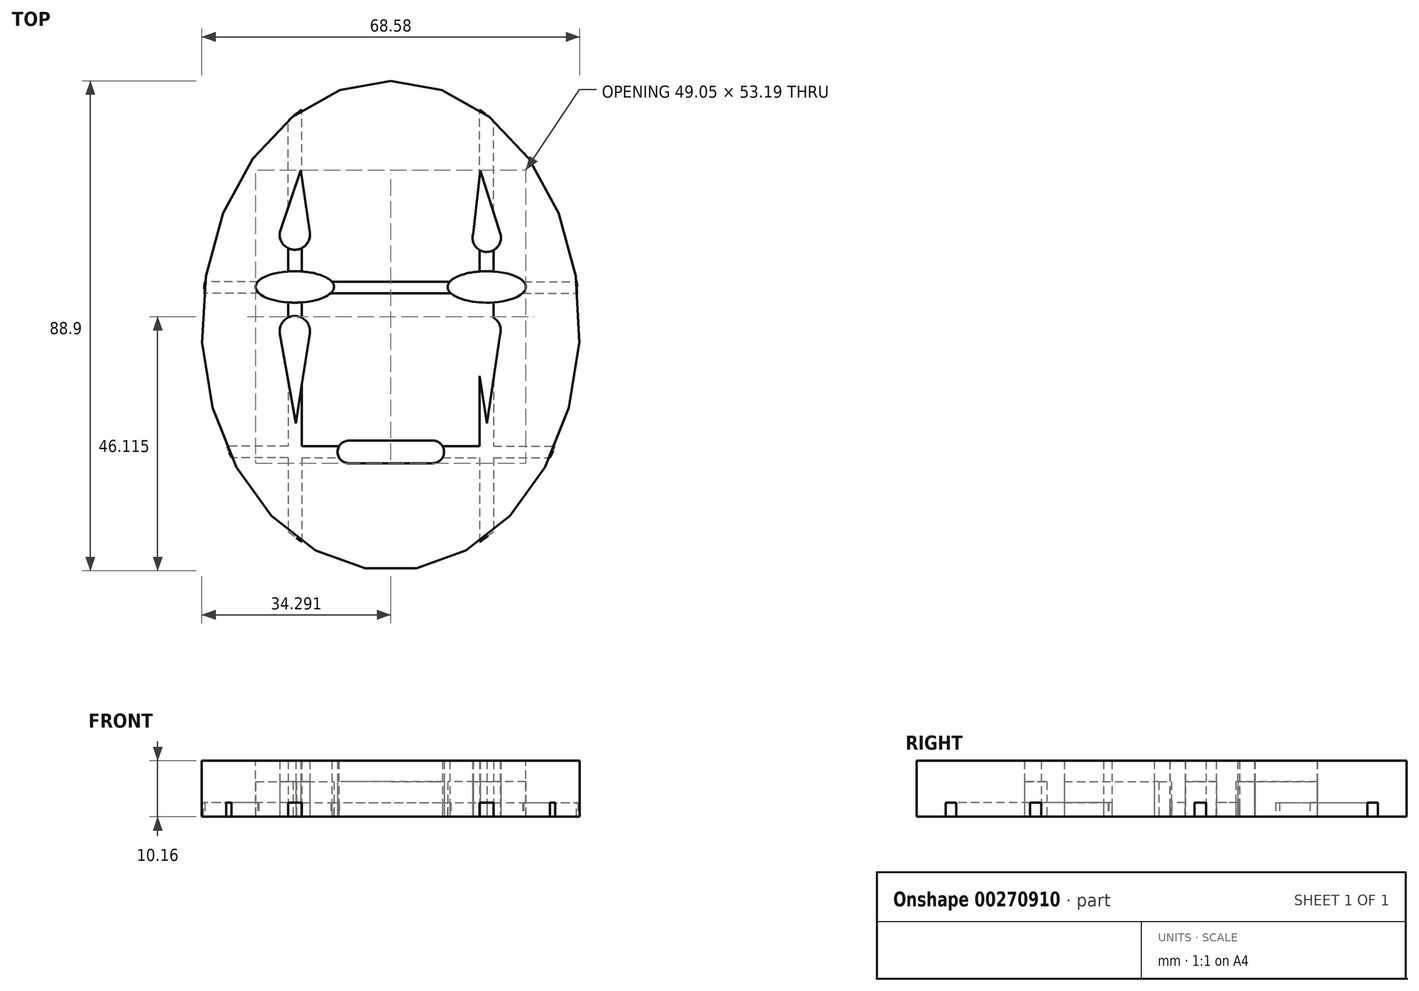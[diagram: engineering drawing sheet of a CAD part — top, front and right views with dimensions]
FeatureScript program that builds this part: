
annotation { "Feature Type Name" : "Feature", "Feature Type Description" : "" }
export const myFeature = defineFeature(function(context is Context, id is Id, definition is map)
    precondition{}
    {
        {
            var Q0;
            Q0=qCreatedBy(makeId("Top.planeOp"),FACE);
            var sketch = newSketch(context, id + "F0", { "sketchPlane" : qUnion([Q0])});
            skEllipse(sketch, "E0", {"center": v(0.89, 1.57) * mm, "majorRadius": 44.45 * mm, "minorRadius": 34.3 * mm, "majorAxis": v(0, 1)});
            skEllipse(sketch, "E1", {"center": v(-16.53, 8.64) * mm, "majorRadius": 7.1 * mm, "minorRadius": 2.85 * mm, "majorAxis": v(-1, 0)});
            skEllipse(sketch, "E2.MirrorC", {"center": v(18.3, 8.64) * mm, "majorRadius": 7.1 * mm, "minorRadius": 2.85 * mm, "majorAxis": v(1, 0)});
            skLineSegment(sketch, "E3.MirrorCS", {"start": v(-15.43, 29.83) * mm, "end": v(-13.8, 18.52) * mm});
            skArc(sketch, "E4", {"start": v(-19.24, 18.52) * mm, "mid": v(-16.52, 15.38) * mm, "end": v(-13.8, 18.52) * mm});
            skLineSegment(sketch, "E5", {"start": v(15.84, 18.38) * mm, "end": v(17.15, 29.74) * mm});
            skLineSegment(sketch, "E6", {"start": v(20.76, 18.36) * mm, "end": v(17.15, 29.74) * mm});
            skArc(sketch, "E7", {"start": v(15.84, 18.38) * mm, "mid": v(18.29, 15) * mm, "end": v(20.76, 18.36) * mm});
            skLineSegment(sketch, "E8", {"start": v(-19.24, 18.52) * mm, "end": v(-15.43, 29.83) * mm});
            skPoint(sketch, "E9.trimOffspring.end.orphan", {"position": v(-33.4, 1.57) * mm});
            skPoint(sketch, "E10.start.orphan", {"position": v(35.18, 1.57) * mm});
            skLineSegment(sketch, "E11", {"start": v(-16.53, 3.36) * mm, "end": v(-16.53, 3.34) * mm});
            skLineSegment(sketch, "E12", {"start": v(-16.33, -16.13) * mm, "end": v(-19.24, 0.19) * mm});
            skLineSegment(sketch, "E13", {"start": v(-16.33, -16.13) * mm, "end": v(-13.8, 0.19) * mm});
            skLineSegment(sketch, "E14", {"start": v(18.3, -16.13) * mm, "end": v(15.84, 0.2) * mm});
            skLineSegment(sketch, "E15", {"start": v(18.3, -16.13) * mm, "end": v(20.76, 0.19) * mm});
            skArc(sketch, "E16", {"start": v(-13.8, 0.19) * mm, "mid": v(-16.53, 3.36) * mm, "end": v(-19.24, 0.19) * mm});
            skArc(sketch, "E17", {"start": v(20.76, 0.19) * mm, "mid": v(18.31, 3.34) * mm, "end": v(15.84, 0.2) * mm});
            skLineSegment(sketch, "E18.trimOffspring", {"start": v(18.3, 3.34) * mm, "end": v(18.3, 3.34) * mm});
            skLineSegment(sketch, "E19.trimOffspring", {"start": v(-13.8, 1.03) * mm, "end": v(-13.8, 0.19) * mm});
            skLineSegment(sketch, "E20.trimOffspring", {"start": v(-16.84, 3.34) * mm, "end": v(-16.22, 3.34) * mm});
            skLineSegment(sketch, "E21.trimOffspring", {"start": v(-19.24, 1.03) * mm, "end": v(-19.24, 0.19) * mm});
            skLineSegment(sketch, "E22.trimOffspring", {"start": v(15.84, 1.41) * mm, "end": v(15.84, 0.2) * mm});
            skLineSegment(sketch, "E23.trimOffspring", {"start": v(20.76, 1.42) * mm, "end": v(20.76, 0.19) * mm});
            skPoint(sketch, "E24", {"position": v(0.9, -19.26) * mm});
            skPoint(sketch, "E25", {"position": v(0.9, -23.36) * mm});
            skLineSegment(sketch, "E26", {"start": v(0.9, -19.26) * mm, "end": v(-6.73, -19.26) * mm});
            skLineSegment(sketch, "E27", {"start": v(0.9, -19.26) * mm, "end": v(8.51, -19.26) * mm});
            skLineSegment(sketch, "E28", {"start": v(0.9, -23.36) * mm, "end": v(-6.73, -23.36) * mm});
            skLineSegment(sketch, "E29", {"start": v(0.9, -23.36) * mm, "end": v(8.51, -23.36) * mm});
            skArc(sketch, "E30", {"start": v(-6.73, -19.26) * mm, "mid": v(-8.78, -21.31) * mm, "end": v(-6.73, -23.36) * mm});
            skArc(sketch, "E31", {"start": v(8.51, -23.36) * mm, "mid": v(10.56, -21.3) * mm, "end": v(8.51, -19.26) * mm});
            skPoint(sketch, "E32.orphan", {"position": v(0.89, 46.02) * mm});
            skPoint(sketch, "E33.orphan", {"position": v(0.89, -42.88) * mm});
            skFitSpline(sketch, "E34.0", {"points": [v(2.64, 46.75) * mm, v(0.89, 46.8) * mm, v(-0.86, 46.75) * mm, v(-3.18, 46.52) * mm, v(-6.04, 45.97) * mm, v(-9.38, 44.88) * mm, v(-12.62, 43.38) * mm, v(-15.72, 41.48) * mm, v(-18.66, 39.2) * mm, v(-20.97, 36.98) * mm, v(-22.72, 35.03) * mm, v(-23.97, 33.48) * mm, v(-25.17, 31.85) * mm, v(-26.67, 29.6) * mm, v(-28.37, 26.62) * mm, v(-30.12, 22.83) * mm, v(-31.57, 18.84) * mm, v(-32.71, 14.7) * mm, v(-33.54, 10.42) * mm, v(-33.97, 6.77) * mm, v(-34.14, 3.81) * mm, v(-34.18, 1.57) * mm, v(-34.14, -0.66) * mm, v(-33.97, -3.62) * mm, v(-33.54, -7.27) * mm, v(-32.71, -11.55) * mm, v(-31.57, -15.7) * mm, v(-30.12, -19.68) * mm, v(-28.37, -23.47) * mm, v(-26.67, -26.45) * mm, v(-25.17, -28.7) * mm, v(-23.97, -30.34) * mm, v(-22.72, -31.89) * mm, v(-20.97, -33.83) * mm, v(-18.66, -36.05) * mm, v(-15.72, -38.33) * mm, v(-12.62, -40.23) * mm, v(-9.38, -41.73) * mm, v(-6.04, -42.82) * mm, v(-3.18, -43.38) * mm, v(-0.86, -43.6) * mm, v(0.89, -43.66) * mm, v(2.64, -43.6) * mm, v(4.96, -43.38) * mm, v(7.81, -42.82) * mm, v(11.16, -41.73) * mm, v(14.4, -40.23) * mm, v(17.5, -38.33) * mm, v(20.44, -36.05) * mm, v(22.75, -33.83) * mm, v(24.5, -31.89) * mm, v(25.75, -30.34) * mm, v(26.94, -28.7) * mm, v(28.44, -26.45) * mm, v(30.14, -23.47) * mm, v(31.9, -19.68) * mm, v(33.34, -15.7) * mm, v(34.49, -11.55) * mm, v(35.32, -7.27) * mm, v(35.74, -3.62) * mm, v(35.91, -0.66) * mm, v(35.95, 1.57) * mm, v(35.91, 3.81) * mm, v(35.74, 6.77) * mm, v(35.32, 10.42) * mm, v(34.49, 14.7) * mm, v(33.34, 18.84) * mm, v(31.9, 22.83) * mm, v(30.14, 26.62) * mm, v(28.44, 29.6) * mm, v(26.94, 31.85) * mm, v(25.75, 33.48) * mm, v(24.5, 35.03) * mm, v(22.75, 36.98) * mm, v(20.44, 39.2) * mm, v(17.5, 41.48) * mm, v(14.4, 43.38) * mm, v(11.16, 44.88) * mm, v(7.81, 45.97) * mm, v(4.96, 46.52) * mm, v(2.64, 46.75) * mm, v(0.89, 46.8) * mm, v(-0.86, 46.75) * mm, v(2.64, 46.75) * mm]});
            skLineSegment(sketch, "E35", {"start": v(-23.23, 9.58) * mm, "end": v(-32.84, 9.58) * mm});
            skLineSegment(sketch, "E36", {"start": v(-23.05, 7.5) * mm, "end": v(-33.1, 7.5) * mm});
            skLineSegment(sketch, "E37", {"start": v(-15.23, 15.7) * mm, "end": v(-15.23, 11.44) * mm});
            skLineSegment(sketch, "E38", {"start": v(-17.75, 15.67) * mm, "end": v(-17.75, 11.45) * mm});
            skLineSegment(sketch, "E39", {"start": v(-15.23, 28.45) * mm, "end": v(-15.23, 40.8) * mm});
            skLineSegment(sketch, "E40", {"start": v(-17.75, 22.94) * mm, "end": v(-17.75, 38.89) * mm});
            skLineSegment(sketch, "E41.MirrorCS", {"start": v(17, 28.5) * mm, "end": v(17, 40.8) * mm});
            skLineSegment(sketch, "E42.MirrorCS", {"start": v(19.52, 22.26) * mm, "end": v(19.52, 38.89) * mm});
            skLineSegment(sketch, "E43.MirrorCS", {"start": v(17, 15.34) * mm, "end": v(17, 11.44) * mm});
            skLineSegment(sketch, "E44.MirrorCS", {"start": v(19.52, 15.3) * mm, "end": v(19.52, 11.45) * mm});
            skLineSegment(sketch, "E45", {"start": v(10.3, -20.3) * mm, "end": v(17, -20.3) * mm});
            skLineSegment(sketch, "E46", {"start": v(10.27, -22.35) * mm, "end": v(17, -22.35) * mm});
            skLineSegment(sketch, "E47.MirrorCS", {"start": v(-17.75, -20.3) * mm, "end": v(-28.96, -20.3) * mm});
            skLineSegment(sketch, "E48.trimOffspring", {"start": v(-17.75, -8.18) * mm, "end": v(-17.75, -20.3) * mm});
            skLineSegment(sketch, "E49.trimOffspring", {"start": v(-15.23, -9.02) * mm, "end": v(-15.23, -20.3) * mm});
            skLineSegment(sketch, "E50.trimOffspring", {"start": v(-15.23, 5.83) * mm, "end": v(-15.23, 3.03) * mm});
            skLineSegment(sketch, "E51.trimOffspring", {"start": v(-9.82, 9.58) * mm, "end": v(11.6, 9.58) * mm});
            skLineSegment(sketch, "E52.trimOffspring", {"start": v(-10, 7.5) * mm, "end": v(11.79, 7.5) * mm});
            skLineSegment(sketch, "E53.trimOffspring", {"start": v(-17.75, 5.83) * mm, "end": v(-17.75, 3.07) * mm});
            skLineSegment(sketch, "E54.trimOffspring", {"start": v(17, -7.48) * mm, "end": v(17, -20.3) * mm});
            skLineSegment(sketch, "E55.trimOffspring", {"start": v(19.52, -8.06) * mm, "end": v(19.52, -20.3) * mm});
            skLineSegment(sketch, "E56.trimOffspring", {"start": v(17, 5.84) * mm, "end": v(17, 2.98) * mm});
            skLineSegment(sketch, "E57.trimOffspring", {"start": v(19.52, 5.83) * mm, "end": v(19.52, 3.03) * mm});
            skLineSegment(sketch, "E58.trimOffspring", {"start": v(25.01, 9.58) * mm, "end": v(34.62, 9.58) * mm});
            skLineSegment(sketch, "E59.trimOffspring", {"start": v(24.83, 7.5) * mm, "end": v(34.87, 7.5) * mm});
            skPoint(sketch, "E60.orphan", {"position": v(19.52, 15.67) * mm});
            skPoint(sketch, "E61.orphan", {"position": v(17, 15.7) * mm});
            skLineSegment(sketch, "E62", {"start": v(-15.23, -20.3) * mm, "end": v(-8.51, -20.3) * mm});
            skLineSegment(sketch, "E63.trimOffspring", {"start": v(-17.75, -22.35) * mm, "end": v(-28.01, -22.35) * mm});
            skLineSegment(sketch, "E64.trimOffspring", {"start": v(-17.75, -22.35) * mm, "end": v(-17.75, -35.74) * mm});
            skLineSegment(sketch, "E65.trimOffspring", {"start": v(17, -22.35) * mm, "end": v(17, -37.66) * mm});
            skLineSegment(sketch, "E66.trimOffspring", {"start": v(19.52, -20.3) * mm, "end": v(30.74, -20.3) * mm});
            skLineSegment(sketch, "E67.trimOffspring", {"start": v(19.52, -22.35) * mm, "end": v(19.52, -35.74) * mm});
            skLineSegment(sketch, "E68.trimOffspring", {"start": v(19.52, -22.35) * mm, "end": v(29.79, -22.35) * mm});
            skPoint(sketch, "E69.endSnap0", {"position": v(-8.78, -21.31) * mm});
            skLineSegment(sketch, "E70", {"start": v(-15.23, -22.35) * mm, "end": v(-8.5, -22.35) * mm});
            skLineSegment(sketch, "E71", {"start": v(-15.23, -22.35) * mm, "end": v(-15.23, -37.66) * mm});
            skSolve(sketch);
        }
        {
            var Q0;
            Q0 = qSketchRegion(id + "F0", true);
            extrude(context, id + "F1", {"entities" : qUnion([Q0]), "depth" : 10.16 * mm});
        }
        {
            var Q0;
            {var subQ0=sQuery(id+"F0.wireOp",EDGE,"E1");var subQ5=makeQuery(id+"F0.imprint","INTERSECT",VERTEX,{"derivedFrom":[subQ0,sQuery(id+"F0.wireOp",EDGE,"E36")]});Q0=makeQuery(id+"F0.imprint","IMPRINT",FACE,{"disambiguationData":[TD([[makeQuery(id+"F0.imprint","IMPRINT",EDGE,{"disambiguationData":[TD([[subQ5,-1.0]])],"derivedFrom":subQ0}),1.0]])]});}
            var Q1;
            {var subQ3=sQuery(id+"F0.wireOp",EDGE,"E8");var subQ5=sQuery(id+"F0.wireOp",EDGE,"E3.MirrorCS");var subQ6=makeQuery(id+"F0.imprint","INTERSECT",VERTEX,{"derivedFrom":[subQ5,subQ3]});Q1=makeQuery(id+"F0.imprint","IMPRINT",FACE,{"disambiguationData":[TD([[makeQuery(id+"F0.imprint","IMPRINT",EDGE,{"disambiguationData":[TD([[subQ6,-1.0]])],"derivedFrom":subQ5}),-1.0]])]});}
            var Q2;
            {var subQ1=sQuery(id+"F0.wireOp",EDGE,"E5");var subQ4=sQuery(id+"F0.wireOp",EDGE,"E7");var subQ7=makeQuery(id+"F0.imprint","INTERSECT",VERTEX,{"derivedFrom":[subQ1,subQ4]});Q2=makeQuery(id+"F0.imprint","IMPRINT",FACE,{"disambiguationData":[TD([[makeQuery(id+"F0.imprint","IMPRINT",EDGE,{"disambiguationData":[TD([[subQ7,-1.0]])],"derivedFrom":subQ1}),-1.0]])]});}
            var Q3;
            {var subQ0=sQuery(id+"F0.wireOp",EDGE,"E2.MirrorC");var subQ4=makeQuery(id+"F0.imprint","INTERSECT",VERTEX,{"derivedFrom":[subQ0,sQuery(id+"F0.wireOp",EDGE,"E44.MirrorCS")]});Q3=makeQuery(id+"F0.imprint","IMPRINT",FACE,{"disambiguationData":[TD([[makeQuery(id+"F0.imprint","IMPRINT",EDGE,{"disambiguationData":[TD([[subQ4,1.0]])],"derivedFrom":subQ0}),1.0]])]});}
            var Q4;
            {var subQ0=sQuery(id+"F0.wireOp",EDGE,"E18.trimOffspring");Q4=makeQuery(id+"F0.imprint","IMPRINT",FACE,{"disambiguationData":[TD([[makeQuery(id+"F0.imprint","IMPRINT",EDGE,{"derivedFrom":subQ0}),-1.0]])]});}
            var Q5;
            {var subQ4=sQuery(id+"F0.wireOp",EDGE,"E19.trimOffspring");Q5=makeQuery(id+"F0.imprint","IMPRINT",FACE,{"disambiguationData":[TD([[makeQuery(id+"F0.imprint","IMPRINT",EDGE,{"derivedFrom":subQ4}),-1.0]])]});}
            var Q6;
            Q6=makeQuery(id+"F0.imprint","IMPRINT",FACE,{"disambiguationData":[TD([[makeQuery(id+"F0.imprint","IMPRINT",EDGE,{"derivedFrom":sQuery(id+"F0.wireOp",EDGE,"E26")}),1.0]])]});
            extrude(context, id + "F2", {"entities" : qUnion([Q0, Q1, Q2, Q3, Q4, Q5, Q6]), "depth" : 6.35 * mm});
        }
        {
            var Q0;
            {var subQ0=sQuery(id+"F0.wireOp",EDGE,"E43.MirrorCS");Q0=makeQuery(id+"F0.imprint","IMPRINT",FACE,{"disambiguationData":[TD([[makeQuery(id+"F0.imprint","IMPRINT",EDGE,{"derivedFrom":subQ0}),1.0]])]});}
            var Q1;
            {var subQ0=sQuery(id+"F0.wireOp",EDGE,"E58.trimOffspring");Q1=makeQuery(id+"F0.imprint","IMPRINT",FACE,{"disambiguationData":[TD([[makeQuery(id+"F0.imprint","IMPRINT",EDGE,{"derivedFrom":subQ0}),-1.0]])]});}
            var Q2;
            {var subQ0=sQuery(id+"F0.wireOp",EDGE,"E51.trimOffspring");Q2=makeQuery(id+"F0.imprint","IMPRINT",FACE,{"disambiguationData":[TD([[makeQuery(id+"F0.imprint","IMPRINT",EDGE,{"derivedFrom":subQ0}),-1.0]])]});}
            var Q3;
            {var subQ0=sQuery(id+"F0.wireOp",EDGE,"E18.trimOffspring");Q3=makeQuery(id+"F0.imprint","IMPRINT",FACE,{"disambiguationData":[TD([[makeQuery(id+"F0.imprint","IMPRINT",EDGE,{"derivedFrom":subQ0}),1.0]])]});}
            var Q4;
            {var subQ1=sQuery(id+"F0.wireOp",EDGE,"E45");Q4=makeQuery(id+"F0.imprint","IMPRINT",FACE,{"disambiguationData":[TD([[makeQuery(id+"F0.imprint","IMPRINT",EDGE,{"derivedFrom":subQ1}),-1.0]])]});}
            var Q5;
            {var subQ2=sQuery(id+"F0.wireOp",EDGE,"E47.MirrorCS");Q5=makeQuery(id+"F0.imprint","IMPRINT",FACE,{"disambiguationData":[TD([[makeQuery(id+"F0.imprint","IMPRINT",EDGE,{"derivedFrom":subQ2}),1.0]])]});}
            var Q6;
            {var subQ0=sQuery(id+"F0.wireOp",EDGE,"E35");Q6=makeQuery(id+"F0.imprint","IMPRINT",FACE,{"disambiguationData":[TD([[makeQuery(id+"F0.imprint","IMPRINT",EDGE,{"derivedFrom":subQ0}),1.0]])]});}
            var Q7;
            {var subQ4=sQuery(id+"F0.wireOp",EDGE,"E50.trimOffspring");Q7=makeQuery(id+"F0.imprint","IMPRINT",FACE,{"disambiguationData":[TD([[makeQuery(id+"F0.imprint","IMPRINT",EDGE,{"derivedFrom":subQ4}),-1.0]])]});}
            var Q8;
            {var subQ0=sQuery(id+"F0.wireOp",EDGE,"E37");Q8=makeQuery(id+"F0.imprint","IMPRINT",FACE,{"disambiguationData":[TD([[makeQuery(id+"F0.imprint","IMPRINT",EDGE,{"derivedFrom":subQ0}),-1.0]])]});}
            var Q9;
            {var subQ4=sQuery(id+"F0.wireOp",EDGE,"E41.MirrorCS");Q9=makeQuery(id+"F0.imprint","IMPRINT",FACE,{"disambiguationData":[TD([[makeQuery(id+"F0.imprint","IMPRINT",EDGE,{"derivedFrom":subQ4}),-1.0]])]});}
            var Q10;
            {var subQ0=sQuery(id+"F0.wireOp",EDGE,"E39");Q10=makeQuery(id+"F0.imprint","IMPRINT",FACE,{"disambiguationData":[TD([[makeQuery(id+"F0.imprint","IMPRINT",EDGE,{"derivedFrom":subQ0}),1.0]])]});}
            extrude(context, id + "F3", {"entities" : qUnion([Q0, Q1, Q2, Q3, Q4, Q5, Q6, Q7, Q8, Q9, Q10]), "depth" : 2.54 * mm});
        }
    });
